# Revit family: LBK-0873xxFSW-0350x840
name_source: partatom
category: Oprawy oświetleniowe
revit_build: Autodesk Revit 2017 (Build: 20190507_1515(x64)
units: mm (PartAtom-declared; Revit-internal decimal feet)

## family parameters
Numer OmniClass = 23.80.70.11
Obiekt nadrzędny = Powierzchnia
Punkt obliczania pomieszczeń = Nie
Tnij formami wycięć po wczytaniu = Nie
Typ części = Normalny
Tytuł OmniClass = Luminaries for Internal Lighting
Współdzielony = Nie
Wymiar okrągłego złącza = Użyj średnicy
Źródło światła = Tak

## types (4) — shared parameters
Emituj kształt widoczny w renderingu = Nie
Emituj z długości prostokąta = 24 mm  [stored 0.0787402 ft]
Emituj z szerokości prostokąta = 843 mm  [stored 2.76575 ft]
Filtr koloru = 16777215
Kod zespołu = D5020200
Lampa = LED
Obciążenie pozorne = 25 VA
Odchylenie kierunku = 90.00°
Producent = RIDI Leuchten GmbH
URL = www.spectral-lighting.com
Zmiana temperatury barwowej przyciemniania lampy = <Brak>
brand = Spectral
conformity mark = CE
electrical safety class = 1
height = 49 mm  [stored 0.160761 ft]
ingress protection (IP) code = IP20
length = 873 mm  [stored 2.86417 ft]
nominal frequency = 50-60Hz
nominal voltage = 230
rated input power = 25
voltage type (AC, DC, UC) = AC
weight = 0.9
width = 24 mm  [stored 0.0787402 ft]
zero-valued in all types: Domyślna rzędna

## per-type parameters (varying)
| type | Model | Plik sieci fotometrycznej |
| LBK 0873NDFSW-0350K840 | SPZ0000066AQ | LBK 1473NDNE-0600K840.IES |
| LBK 0873DAFSW-0350K840 | SPZ0000067AQ | LBK 1473NDNE-0600K840.IES |
| LBK 0873NDFSW-0350O840 | SPZ0000070AQ | LBK 1473NDNE-0600O840.IES |
| LBK 0873DAFSW-0350O840 | SPZ0000071AQ | LBK 1473NDNE-0600O840.IES |

note: column(s) folded — value = type name in every type: product name

note: [stored X ft] marks values corroborated as IEEE doubles in the binary element streams (Revit-internal decimal feet)
